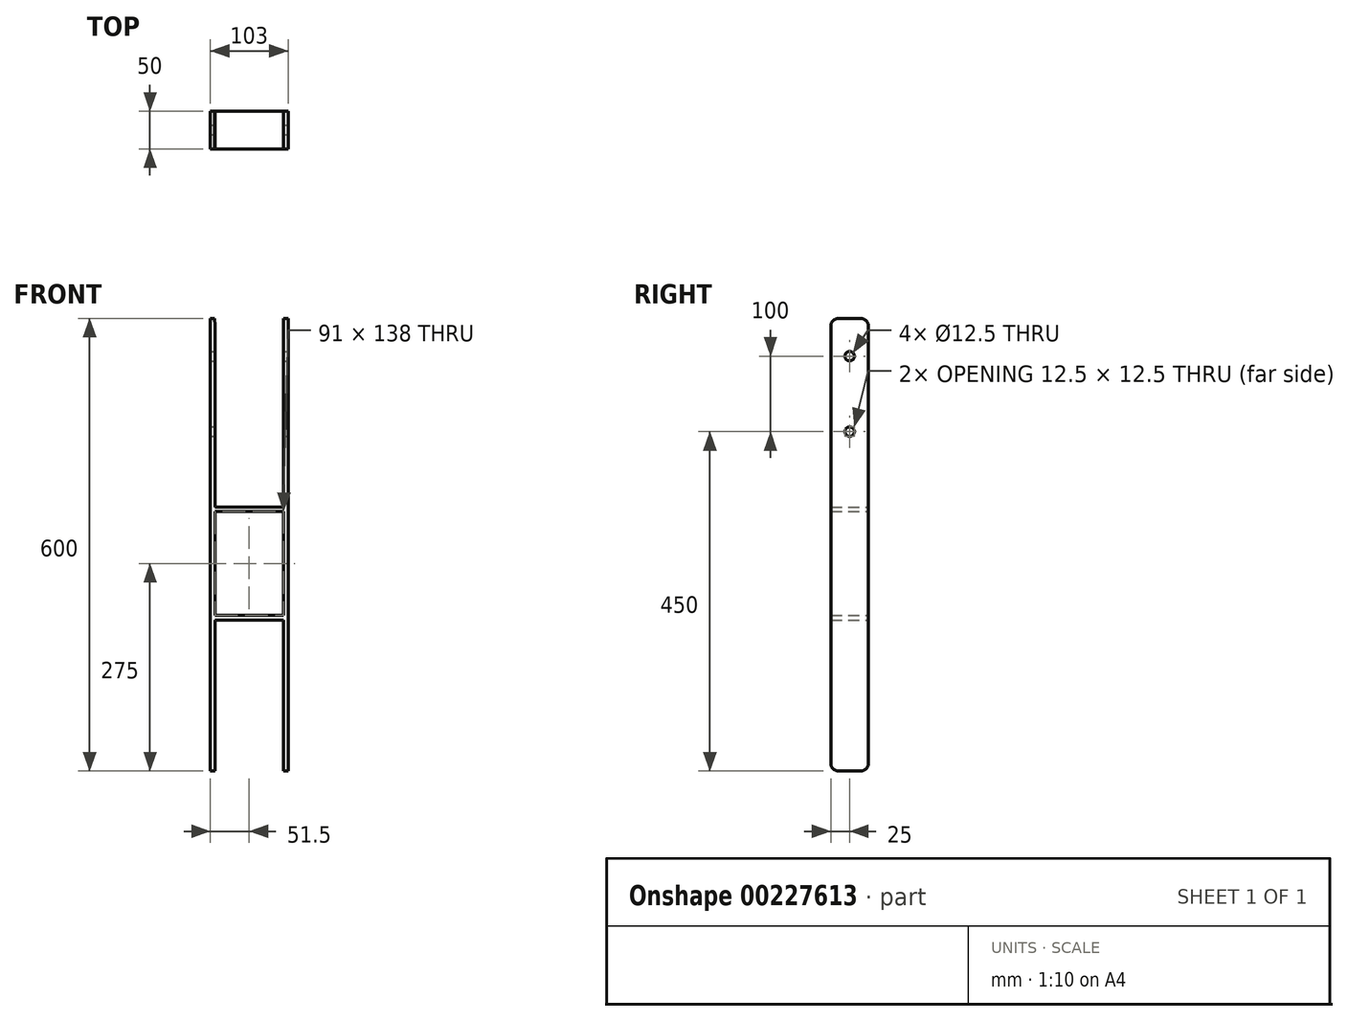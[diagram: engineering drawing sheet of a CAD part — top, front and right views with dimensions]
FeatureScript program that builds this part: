
annotation { "Feature Type Name" : "Feature", "Feature Type Description" : "" }
export const myFeature = defineFeature(function(context is Context, id is Id, definition is map)
    precondition{}
    {
        {
            var Q0;
            Q0=qCreatedBy(makeId("Front.planeOp"),FACE);
            var sketch = newSketch(context, id + "F0", { "sketchPlane" : qUnion([Q0])});
            skLineSegment(sketch, "E0", {"start": v(-200.62, 0) * mm, "end": v(200.75, 0) * mm, "construction": true});
            skLineSegment(sketch, "E1", {"start": v(0, -177.39) * mm, "end": v(0, 159.8) * mm, "construction": true});
            skLineSegment(sketch, "E2", {"start": v(-45.5, 0) * mm, "end": v(45.5, 0) * mm});
            skLineSegment(sketch, "E3", {"start": v(45.5, 0) * mm, "end": v(45.5, 250) * mm});
            skLineSegment(sketch, "E4", {"start": v(45.5, 250) * mm, "end": v(51.5, 250) * mm});
            skLineSegment(sketch, "E5", {"start": v(51.5, 250) * mm, "end": v(51.5, -350) * mm});
            skLineSegment(sketch, "E6", {"start": v(51.5, -350) * mm, "end": v(45.5, -350) * mm});
            skLineSegment(sketch, "E7", {"start": v(45.5, -350) * mm, "end": v(45.5, -150) * mm});
            skLineSegment(sketch, "E8", {"start": v(45.5, -150) * mm, "end": v(-45.5, -150) * mm});
            skLineSegment(sketch, "E9", {"start": v(-45.5, -150) * mm, "end": v(-45.5, -350) * mm});
            skLineSegment(sketch, "E10", {"start": v(-45.5, -350) * mm, "end": v(-51.5, -350) * mm});
            skLineSegment(sketch, "E11", {"start": v(-51.5, -350) * mm, "end": v(-51.5, 250) * mm});
            skLineSegment(sketch, "E12", {"start": v(-51.5, 250) * mm, "end": v(-45.7, 250) * mm});
            skLineSegment(sketch, "E13", {"start": v(-45.7, 250) * mm, "end": v(-45.5, 0) * mm});
            skLineSegment(sketch, "E14.bottom", {"start": v(-45.5, -6) * mm, "end": v(45.5, -6) * mm});
            skLineSegment(sketch, "E14.top", {"start": v(-45.5, -144) * mm, "end": v(45.5, -144) * mm});
            skLineSegment(sketch, "E14.left", {"start": v(-45.5, -6) * mm, "end": v(-45.5, -144) * mm});
            skLineSegment(sketch, "E14.right", {"start": v(45.5, -6) * mm, "end": v(45.5, -144) * mm});
            skSolve(sketch);
        }
        {
            var Q0;
            Q0=qSketchRegion(id+"F0",true);
            extrude(context, id + "F1", {"entities" : qUnion([Q0]), "endBound" : BoundingType.SYMMETRIC, "depth" : 50 * mm});
        }
        {
            var Q0;
            Q0=makeQuery(id+"F1.opExtrude","CAP_EDGE",EDGE,{"disambiguationData":[OSD([sQuery(id+"F0.wireOp",EDGE,"E4")])],"isStart":false});
            var Q1;
            Q1=makeQuery(id+"F1.opExtrude","CAP_EDGE",EDGE,{"disambiguationData":[OSD([sQuery(id+"F0.wireOp",EDGE,"E4")])],"isStart":true});
            var Q2;
            Q2=makeQuery(id+"F1.opExtrude","CAP_EDGE",EDGE,{"disambiguationData":[OSD([sQuery(id+"F0.wireOp",EDGE,"E12")])],"isStart":false});
            var Q3;
            Q3=makeQuery(id+"F1.opExtrude","CAP_EDGE",EDGE,{"disambiguationData":[OSD([sQuery(id+"F0.wireOp",EDGE,"E12")])],"isStart":true});
            var Q4;
            Q4=makeQuery(id+"F1.opExtrude","CAP_EDGE",EDGE,{"disambiguationData":[OSD([sQuery(id+"F0.wireOp",EDGE,"E6")])],"isStart":false});
            var Q5;
            Q5=makeQuery(id+"F1.opExtrude","CAP_EDGE",EDGE,{"disambiguationData":[OSD([sQuery(id+"F0.wireOp",EDGE,"E10")])],"isStart":false});
            var Q6;
            Q6=makeQuery(id+"F1.opExtrude","CAP_EDGE",EDGE,{"disambiguationData":[OSD([sQuery(id+"F0.wireOp",EDGE,"E6")])],"isStart":true});
            var Q7;
            Q7=makeQuery(id+"F1.opExtrude","CAP_EDGE",EDGE,{"disambiguationData":[OSD([sQuery(id+"F0.wireOp",EDGE,"E10")])],"isStart":true});
            fillet(context, id + "F2", {"entities" : qUnion([Q0, Q1, Q2, Q3, Q4, Q5, Q6, Q7]), "radius" : 10 * mm, "tangentPropagation" : true, "allowEdgeOverflow" : false});
        }
        {
            var Q0;
            Q0=makeQuery(id+"F1.opExtrude","SWEPT_FACE",FACE,{"disambiguationData":[OSD([sQuery(id+"F0.wireOp",EDGE,"E5")])]});
            var sketch = newSketch(context, id + "F3", { "sketchPlane" : qUnion([Q0])});
            skLineSegment(sketch, "E15", {"start": v(0, 0) * mm, "end": v(0, 250) * mm, "construction": true});
            skCircle(sketch, "E16", {"center": v(0, 200) * mm, "radius": 6.25 * mm});
            skCircle(sketch, "E17", {"center": v(0, 100) * mm, "radius": 6.25 * mm});
            skSolve(sketch);
        }
        {
            var Q0;
            Q0=qSketchRegion(id+"F3",true);
            extrude(context, id + "F4", {"entities" : qUnion([Q0]), "operationType" : NewBodyOperationType.REMOVE, "endBound" : BoundingType.THROUGH_ALL, "oppositeDirection" : true, "depth" : 25 * mm});
        }
    });
